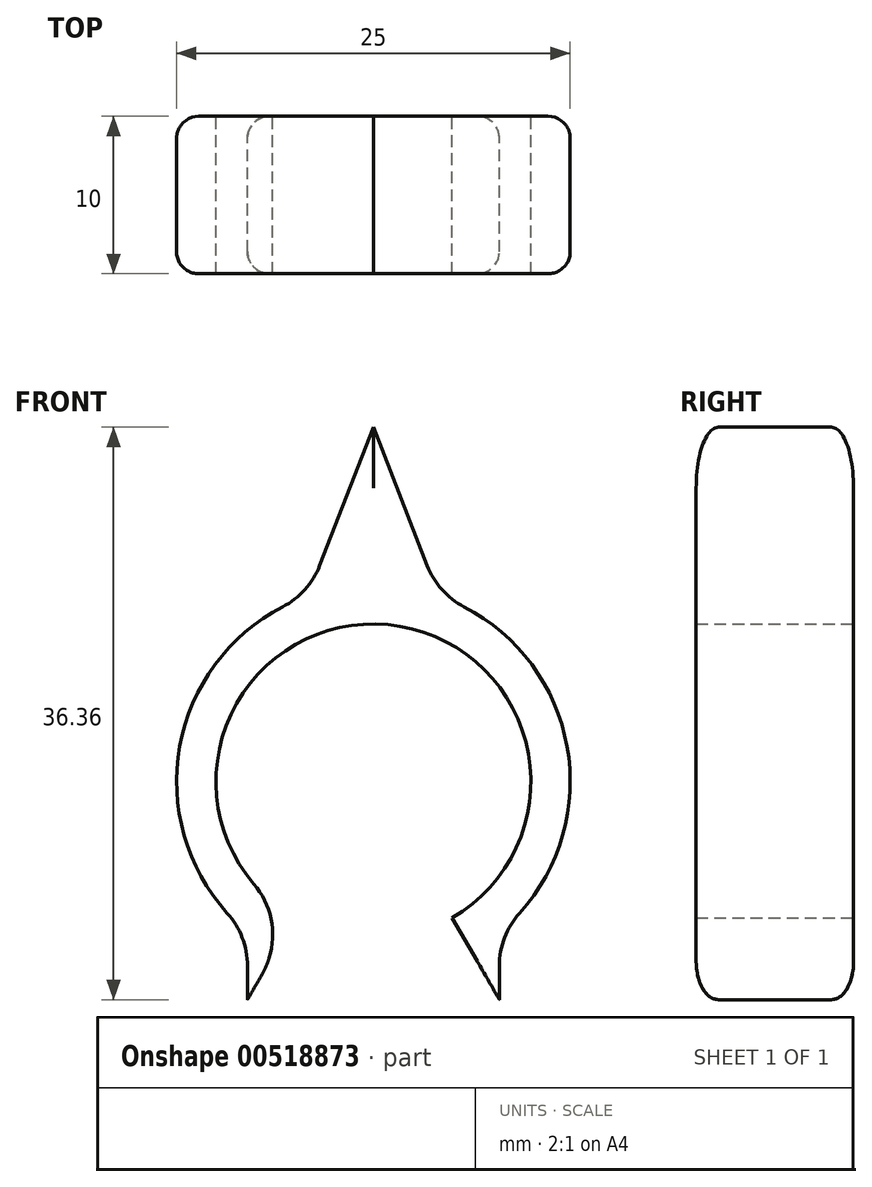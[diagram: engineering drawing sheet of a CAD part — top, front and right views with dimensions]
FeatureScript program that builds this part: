
annotation { "Feature Type Name" : "Feature", "Feature Type Description" : "" }
export const myFeature = defineFeature(function(context is Context, id is Id, definition is map)
    precondition{}
    {
        {
            var Q0;
            Q0=qCreatedBy(makeId("Front.planeOp"),FACE);
            var sketch = newSketch(context, id + "F0", { "sketchPlane" : qUnion([Q0])});
            skArc(sketch, "E0", {"start": v(5, -8.66) * mm, "mid": v(0, 10) * mm, "end": v(-5, -8.66) * mm});
            skArc(sketch, "E1", {"start": v(8, -9.6) * mm, "mid": v(0, 12.5) * mm, "end": v(-8, -9.6) * mm});
            skLineSegment(sketch, "E2", {"start": v(-5, -8.66) * mm, "end": v(-6.25, -10.83) * mm});
            skLineSegment(sketch, "E3", {"start": v(5, -8.66) * mm, "end": v(6.25, -10.83) * mm});
            skLineSegment(sketch, "E4", {"start": v(4.16, 11.79) * mm, "end": v(0, 22.5) * mm});
            skLineSegment(sketch, "E5", {"start": v(0, 22.5) * mm, "end": v(-4.16, 11.79) * mm});
            skLineSegment(sketch, "E6", {"start": v(-5, -8.66) * mm, "end": v(-8, -13.86) * mm});
            skLineSegment(sketch, "E7", {"start": v(-8, -13.86) * mm, "end": v(-8, -9.6) * mm});
            skLineSegment(sketch, "E8", {"start": v(5, -8.66) * mm, "end": v(8, -13.86) * mm});
            skLineSegment(sketch, "E9", {"start": v(8, -13.86) * mm, "end": v(8, -9.6) * mm});
            skPoint(sketch, "E10.trimOffspring.end.orphan", {"position": v(-8, 0) * mm});
            skPoint(sketch, "E11.trimOffspring.end.orphan", {"position": v(8, 0) * mm});
            skSolve(sketch);
        }
        {
            var Q0;
            Q0=qSketchRegion(id+"F0",true);
            extrude(context, id + "F1", {"entities" : qUnion([Q0]), "depth" : 10 * mm, "offsetDistance" : 25 * mm});
        }
        {
            var Q0;
            Q0=makeQuery(id+"F1.opExtrude","SWEPT_EDGE",EDGE,{"disambiguationData":[OSD([sQuery(id+"F0.wireOp",EDGE,"E1"),sQuery(id+"F0.wireOp",EDGE,"E5")])]});
            fillet(context, id + "F2", {"entities" : qUnion([Q0]), "radius" : 5 * mm, "tangentPropagation" : true, "allowEdgeOverflow" : false});
        }
        {
            var Q0;
            Q0=makeQuery(id+"F1.opExtrude","SWEPT_EDGE",EDGE,{"disambiguationData":[OSD([sQuery(id+"F0.wireOp",EDGE,"E1"),sQuery(id+"F0.wireOp",EDGE,"E4")])]});
            fillet(context, id + "F3", {"entities" : qUnion([Q0]), "radius" : 5 * mm, "tangentPropagation" : true, "allowEdgeOverflow" : false});
        }
        {
            var Q0;
            Q0=makeQuery(id+"F1.opExtrude","SWEPT_EDGE",EDGE,{"disambiguationData":[OSD([sQuery(id+"F0.wireOp",EDGE,"E0"),sQuery(id+"F0.wireOp",EDGE,"E2")])]});
            fillet(context, id + "F4", {"entities" : qUnion([Q0]), "radius" : 5 * mm, "tangentPropagation" : true, "allowEdgeOverflow" : false});
        }
        {
            var Q0;
            Q0=makeQuery(id+"F1.opExtrude","SWEPT_EDGE",EDGE,{"disambiguationData":[OSD([sQuery(id+"F0.wireOp",EDGE,"E1"),sQuery(id+"F0.wireOp",EDGE,"E7")])]});
            fillet(context, id + "F5", {"entities" : qUnion([Q0]), "radius" : 5 * mm, "tangentPropagation" : true, "allowEdgeOverflow" : false});
        }
        {
            var Q0;
            Q0=makeQuery(id+"F1.opExtrude","SWEPT_EDGE",EDGE,{"disambiguationData":[OSD([sQuery(id+"F0.wireOp",EDGE,"E1"),sQuery(id+"F0.wireOp",EDGE,"E9")])]});
            fillet(context, id + "F6", {"entities" : qUnion([Q0]), "radius" : 5 * mm, "tangentPropagation" : true, "allowEdgeOverflow" : false});
        }
        {
            var Q0;
            Q0=makeQuery(id+"F1.opExtrude","CAP_EDGE",EDGE,{"disambiguationData":[OSD([sQuery(id+"F0.wireOp",EDGE,"E4")])],"isStart":false});
            var Q1;
            Q1=makeQuery(id+"F1.opExtrude","CAP_EDGE",EDGE,{"disambiguationData":[OSD([sQuery(id+"F0.wireOp",EDGE,"E5")])],"isStart":false});
            fillet(context, id + "F7", {"entities" : qUnion([Q0, Q1]), "radius" : 1.4 * mm, "tangentPropagation" : true, "allowEdgeOverflow" : false});
        }
        {
            var Q0;
            Q0=makeQuery(id+"F1.opExtrude","CAP_EDGE",EDGE,{"disambiguationData":[OSD([sQuery(id+"F0.wireOp",EDGE,"E4")])],"isStart":true});
            var Q1;
            Q1=makeQuery(id+"F1.opExtrude","CAP_EDGE",EDGE,{"disambiguationData":[OSD([sQuery(id+"F0.wireOp",EDGE,"E5")])],"isStart":true});
            fillet(context, id + "F8", {"entities" : qUnion([Q0, Q1]), "radius" : 1.4 * mm, "tangentPropagation" : true, "allowEdgeOverflow" : false});
        }
    });
